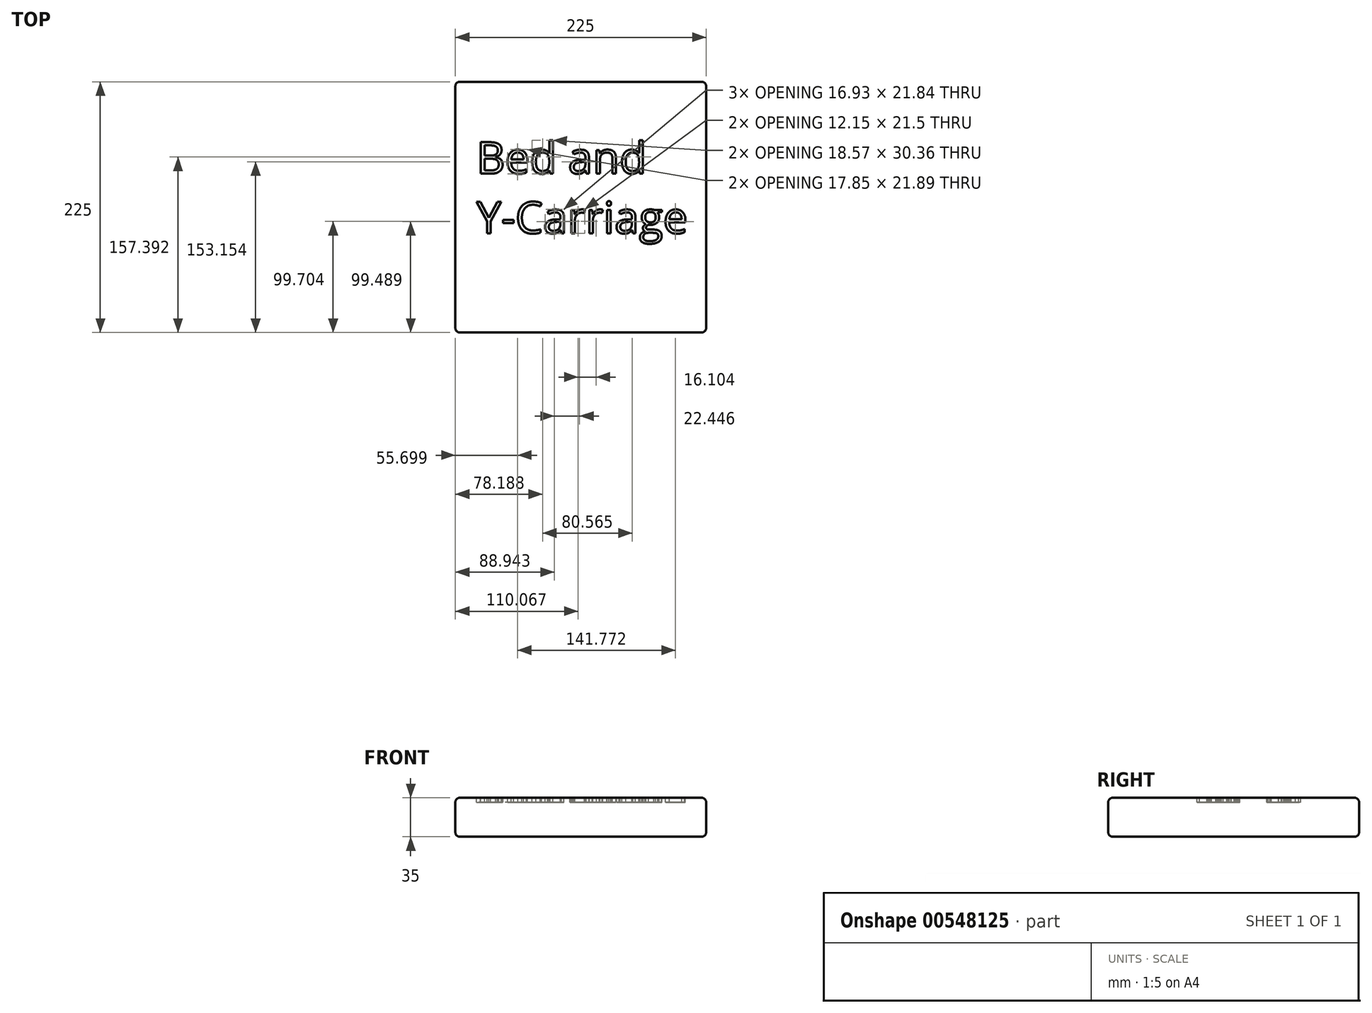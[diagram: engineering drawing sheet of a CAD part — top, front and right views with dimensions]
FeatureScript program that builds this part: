
annotation { "Feature Type Name" : "Feature", "Feature Type Description" : "" }
export const myFeature = defineFeature(function(context is Context, id is Id, definition is map)
    precondition{}
    {
        {
            var Q0;
            Q0=qCreatedBy(makeId("Top.planeOp"),FACE);
            var sketch = newSketch(context, id + "F0", { "sketchPlane" : qUnion([Q0])});
            skLineSegment(sketch, "E0.bottom", {"start": v(0, 0) * mm, "end": v(-225, 0) * mm});
            skLineSegment(sketch, "E0.top", {"start": v(0, 225) * mm, "end": v(-225, 225) * mm});
            skLineSegment(sketch, "E0.left", {"start": v(0, 0) * mm, "end": v(0, 225) * mm});
            skLineSegment(sketch, "E0.right", {"start": v(-225, 0) * mm, "end": v(-225, 225) * mm});
            skSolve(sketch);
        }
        {
            var Q0;
            Q0=makeQuery(id+"F0.imprint","IMPRINT",FACE,{"disambiguationData":[TD([[makeQuery(id+"F0.imprint","IMPRINT",EDGE,{"derivedFrom":sQuery(id+"F0.wireOp",EDGE,"E0.bottom")}),-1.0]])]});
            extrude(context, id + "F1", {"entities" : qUnion([Q0]), "depth" : 35 * mm, "offsetDistance" : 25 * mm});
        }
        {
            var Q0;
            Q0=makeQuery(id+"F1.opExtrude","SWEPT_FACE",FACE,{"disambiguationData":[OSD([sQuery(id+"F0.wireOp",EDGE,"E0.bottom")])]});
            var Q1;
            Q1=makeQuery(id+"F1.opExtrude","SWEPT_FACE",FACE,{"disambiguationData":[OSD([sQuery(id+"F0.wireOp",EDGE,"E0.left")])]});
            var Q2;
            Q2=makeQuery(id+"F1.opExtrude","CAP_FACE",FACE,{"disambiguationData":[OSD([sQuery(id+"F0.wireOp",EDGE,"E0.bottom"),sQuery(id+"F0.wireOp",EDGE,"E0.top"),sQuery(id+"F0.wireOp",EDGE,"E0.left"),sQuery(id+"F0.wireOp",EDGE,"E0.right")])],"isStart":false});
            var Q3;
            Q3=makeQuery(id+"F1.opExtrude","SWEPT_FACE",FACE,{"disambiguationData":[OSD([sQuery(id+"F0.wireOp",EDGE,"E0.right")])]});
            var Q4;
            Q4=makeQuery(id+"F1.opExtrude","SWEPT_FACE",FACE,{"disambiguationData":[OSD([sQuery(id+"F0.wireOp",EDGE,"E0.top")])]});
            var Q5;
            Q5=makeQuery(id+"F1.opExtrude","CAP_FACE",FACE,{"disambiguationData":[OSD([sQuery(id+"F0.wireOp",EDGE,"E0.bottom"),sQuery(id+"F0.wireOp",EDGE,"E0.top"),sQuery(id+"F0.wireOp",EDGE,"E0.left"),sQuery(id+"F0.wireOp",EDGE,"E0.right")])],"isStart":true});
            fillet(context, id + "F2", {"entities" : qUnion([Q0, Q1, Q2, Q3, Q4, Q5]), "radius" : 4 * mm, "tangentPropagation" : true, "allowEdgeOverflow" : false});
        }
        {
            var Q0;
            Q0=makeQuery(id+"F1.opExtrude","CAP_FACE",FACE,{"disambiguationData":[OSD([sQuery(id+"F0.wireOp",EDGE,"E0.bottom"),sQuery(id+"F0.wireOp",EDGE,"E0.top"),sQuery(id+"F0.wireOp",EDGE,"E0.left"),sQuery(id+"F0.wireOp",EDGE,"E0.right")])],"isStart":false});
            var sketch = newSketch(context, id + "F3", { "sketchPlane" : qUnion([Q0])});
            skText(sketch, "E1", { "text": "Bed and \nY-Carriage", "fontName": "OpenSans-Regular.ttf"});
            const initialGuessF3  = {"E1": [-0.206, 0.1426, 1, 0, 0.0284]};
            skSetInitialGuess(sketch, initialGuessF3);
            skSolve(sketch);
        }
        {
            var Q0;
            Q0 = qSketchRegion(id + "F3", true);
            extrude(context, id + "F4", {"entities" : qUnion([Q0]), "operationType" : NewBodyOperationType.REMOVE, "oppositeDirection" : true, "depth" : 4 * mm, "offsetDistance" : 25 * mm});
        }
    });
